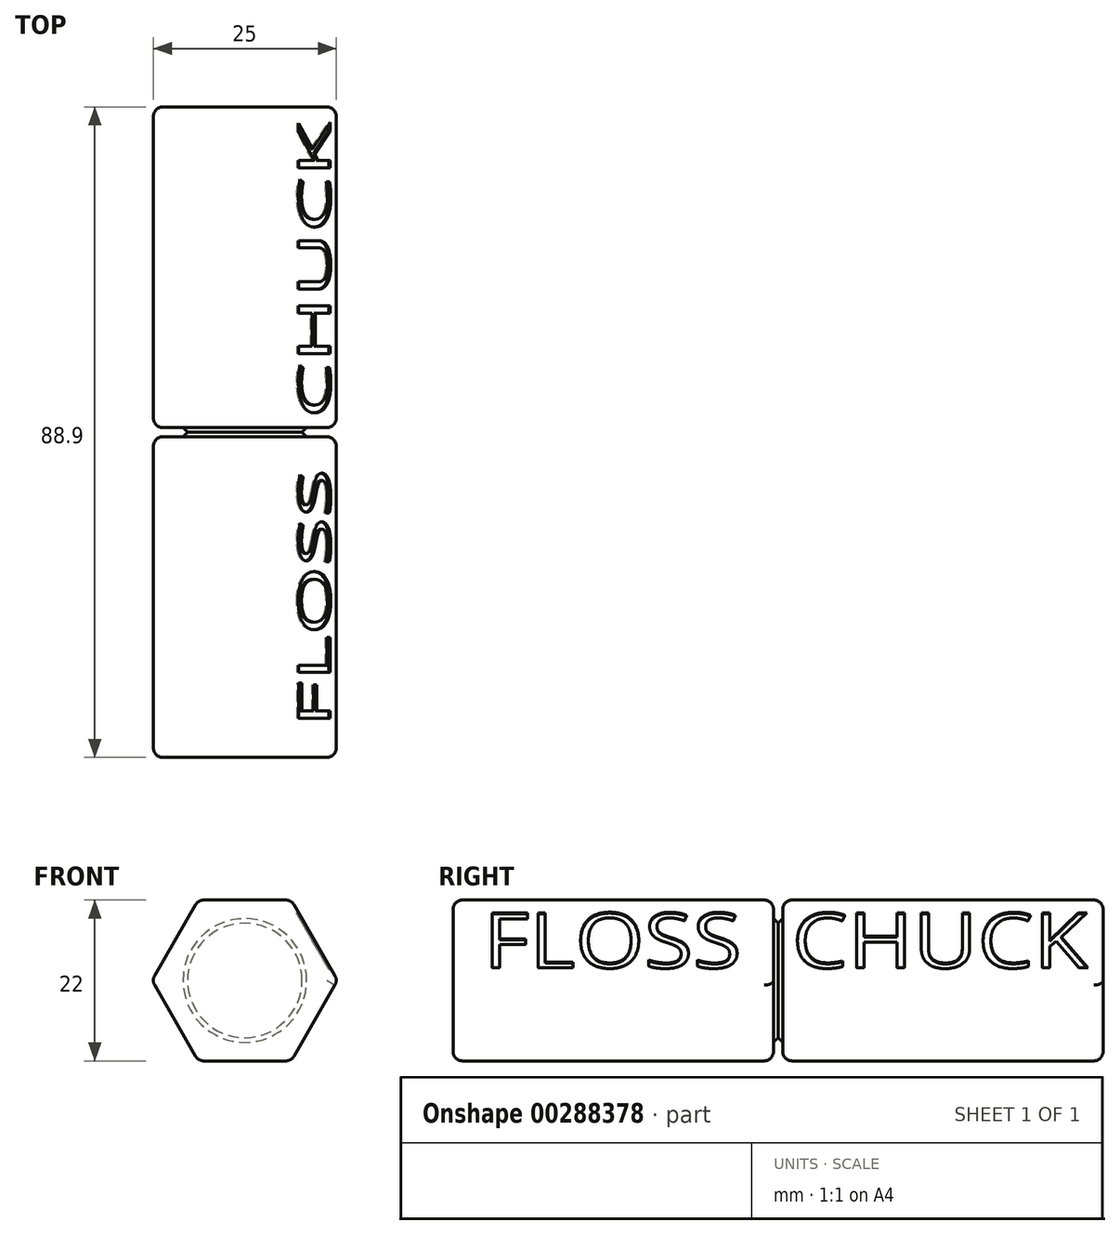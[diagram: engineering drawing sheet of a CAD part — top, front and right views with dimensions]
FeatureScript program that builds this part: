
annotation { "Feature Type Name" : "Feature", "Feature Type Description" : "" }
export const myFeature = defineFeature(function(context is Context, id is Id, definition is map)
    precondition{}
    {
        {
            var Q0;
            Q0=qCreatedBy(makeId("Front.planeOp"),FACE);
            var sketch = newSketch(context, id + "F0", { "sketchPlane" : qUnion([Q0])});
            skCircle(sketch, "E0.cCircle", {"center": v(0, 0) * mm, "radius": 12.7 * mm, "construction": true});
            skLineSegment(sketch, "E0.0", {"start": v(12.33, -0.64) * mm, "end": v(6.72, -10.36) * mm});
            skLineSegment(sketch, "E0.1", {"start": v(5.62, -11) * mm, "end": v(-5.62, -11) * mm});
            skLineSegment(sketch, "E0.2", {"start": v(-6.72, -10.36) * mm, "end": v(-12.33, -0.63) * mm});
            skLineSegment(sketch, "E0.3", {"start": v(-12.33, 0.64) * mm, "end": v(-6.72, 10.36) * mm});
            skLineSegment(sketch, "E0.4", {"start": v(-5.62, 11) * mm, "end": v(5.62, 11) * mm});
            skLineSegment(sketch, "E0.5", {"start": v(6.72, 10.36) * mm, "end": v(12.33, 0.63) * mm});
            skPoint(sketch, "E1.visualSharp", {"position": v(-6.35, 11) * mm});
            skArc(sketch, "E1.filletArc", {"start": v(-5.62, 11) * mm, "mid": v(-6.25, 10.83) * mm, "end": v(-6.72, 10.36) * mm});
            skPoint(sketch, "E2.visualSharp", {"position": v(6.35, 11) * mm});
            skArc(sketch, "E2.filletArc", {"start": v(6.72, 10.36) * mm, "mid": v(6.25, 10.83) * mm, "end": v(5.62, 11) * mm});
            skPoint(sketch, "E3.visualSharp", {"position": v(12.7, 0) * mm});
            skArc(sketch, "E3.filletArc", {"start": v(12.33, -0.64) * mm, "mid": v(12.5, 0) * mm, "end": v(12.33, 0.63) * mm});
            skPoint(sketch, "E4.visualSharp", {"position": v(6.35, -11) * mm});
            skArc(sketch, "E4.filletArc", {"start": v(5.62, -11) * mm, "mid": v(6.25, -10.83) * mm, "end": v(6.72, -10.36) * mm});
            skPoint(sketch, "E5.visualSharp", {"position": v(-6.35, -11) * mm});
            skArc(sketch, "E5.filletArc", {"start": v(-6.72, -10.36) * mm, "mid": v(-6.25, -10.83) * mm, "end": v(-5.62, -11) * mm});
            skPoint(sketch, "E6.visualSharp", {"position": v(-12.7, 0) * mm});
            skArc(sketch, "E6.filletArc", {"start": v(-12.33, 0.64) * mm, "mid": v(-12.5, 0) * mm, "end": v(-12.33, -0.63) * mm});
            skSolve(sketch);
        }
        {
            var Q0;
            Q0=makeQuery(id+"F0.imprint","IMPRINT",FACE,{"disambiguationData":[TD([[makeQuery(id+"F0.imprint","IMPRINT",EDGE,{"derivedFrom":sQuery(id+"F0.wireOp",EDGE,"E0.0")}),-1.0]])]});
            extrude(context, id + "F1", {"entities" : qUnion([Q0]), "depth" : 88.9 * mm, "symmetric" : true});
        }
        {
            var Q0;
            Q0=qCreatedBy(makeId("Front.planeOp"),FACE);
            var sketch = newSketch(context, id + "F2", { "sketchPlane" : qUnion([Q0])});
            skCircle(sketch, "E7.0", {"center": v(0, 0) * mm, "radius": 14.17 * mm});
            skCircle(sketch, "E8.0", {"center": v(0, 0) * mm, "radius": 7.82 * mm});
            skSolve(sketch);
        }
        {
            var Q0;
            Q0 = qSketchRegion(id + "F2", true);
            extrude(context, id + "F3", {"entities" : qUnion([Q0]), "operationType" : NewBodyOperationType.REMOVE, "oppositeDirection" : true, "depth" : 1.27 * mm, "symmetric" : true});
        }
        {
            var Q0;
            Q0=makeQuery(id+"F3.boolean.opBoolean","COPY",FACE,{"derivedFrom":makeQuery(id+"F3.opExtrude","SWEPT_FACE",FACE,{"disambiguationData":[OSD([sQuery(id+"F2.wireOp",EDGE,"E8.0")])]})});
            chamfer(context, id + "F4", {"entities" : qUnion([Q0]), "width" : 0.64 * mm, "tangentPropagation" : true});
        }
        {
            var Q0;
            Q0=makeQuery(id+"F3.boolean.opBoolean","INTERSECT",EDGE,{"derivedFrom":[makeQuery(id+"F1.opExtrude","SWEPT_FACE",FACE,{"disambiguationData":[OSD([sQuery(id+"F0.wireOp",EDGE,"E0.1")])]}),makeQuery(id+"F3.opExtrude","CAP_FACE",FACE,{"disambiguationData":[OSD([sQuery(id+"F2.wireOp",EDGE,"E7.0"),sQuery(id+"F2.wireOp",EDGE,"E8.0")])],"isStart":false})]});
            var Q1;
            Q1=makeQuery(id+"F3.boolean.opBoolean","INTERSECT",EDGE,{"derivedFrom":[makeQuery(id+"F1.opExtrude","SWEPT_FACE",FACE,{"disambiguationData":[OSD([sQuery(id+"F0.wireOp",EDGE,"E0.1")])]}),makeQuery(id+"F3.opExtrude","CAP_FACE",FACE,{"disambiguationData":[OSD([sQuery(id+"F2.wireOp",EDGE,"E7.0"),sQuery(id+"F2.wireOp",EDGE,"E8.0")])],"isStart":true})]});
            fillet(context, id + "F5", {"entities" : qUnion([Q0, Q1]), "radius" : 1.27 * mm, "tangentPropagation" : true, "allowEdgeOverflow" : false});
        }
        {
            var Q0;
            Q0=makeQuery(id+"F1.opExtrude","CAP_EDGE",EDGE,{"disambiguationData":[OSD([sQuery(id+"F0.wireOp",EDGE,"E0.1")])],"isStart":false});
            var Q1;
            Q1=makeQuery(id+"F1.opExtrude","CAP_EDGE",EDGE,{"disambiguationData":[OSD([sQuery(id+"F0.wireOp",EDGE,"E0.1")])],"isStart":true});
            fillet(context, id + "F6", {"entities" : qUnion([Q0, Q1]), "radius" : 1.27 * mm, "tangentPropagation" : true, "allowEdgeOverflow" : false});
        }
        {
            var Q0;
            {var subQ2=sQuery(id+"F0.wireOp",EDGE,"E0.5");Q0=makeQuery(id+"F3.boolean.opBoolean","SPLIT",FACE,{"disambiguationData":[TD([makeQuery(id+"F3.opExtrude","CAP_FACE",FACE,{"disambiguationData":[OSD([sQuery(id+"F2.wireOp",EDGE,"E7.0"),sQuery(id+"F2.wireOp",EDGE,"E8.0")])],"isStart":true})])],"derivedFrom":makeQuery(id+"F1.opExtrude","SWEPT_FACE",FACE,{"disambiguationData":[OSD([subQ2])]})});}
            var sketch = newSketch(context, id + "F7", { "sketchPlane" : qUnion([Q0])});
            skText(sketch, "E9", { "text": "FLOSS", "fontName": "OpenSans-Regular.ttf"});
            skText(sketch, "E10", { "text": "CHUCK", "fontName": "OpenSans-Regular.ttf"});
            skPoint(sketch, "E11", {"position": v(-22.54, 0) * mm});
            const initialGuessF7  = {"E9": [-0.04029, -0.00436, 1, 0, 0.00872], "E10": [0.0019, -0.00436, 1, 0, 0.00872]};
            skSetInitialGuess(sketch, initialGuessF7);
            skSolve(sketch);
        }
        {
            var Q0;
            Q0 = qSketchRegion(id + "F7", true);
            extrude(context, id + "F8", {"entities" : qUnion([Q0]), "operationType" : NewBodyOperationType.REMOVE, "oppositeDirection" : true, "depth" : .25 * mm, "offsetDistance" : 25.4 * mm});
        }
    });
